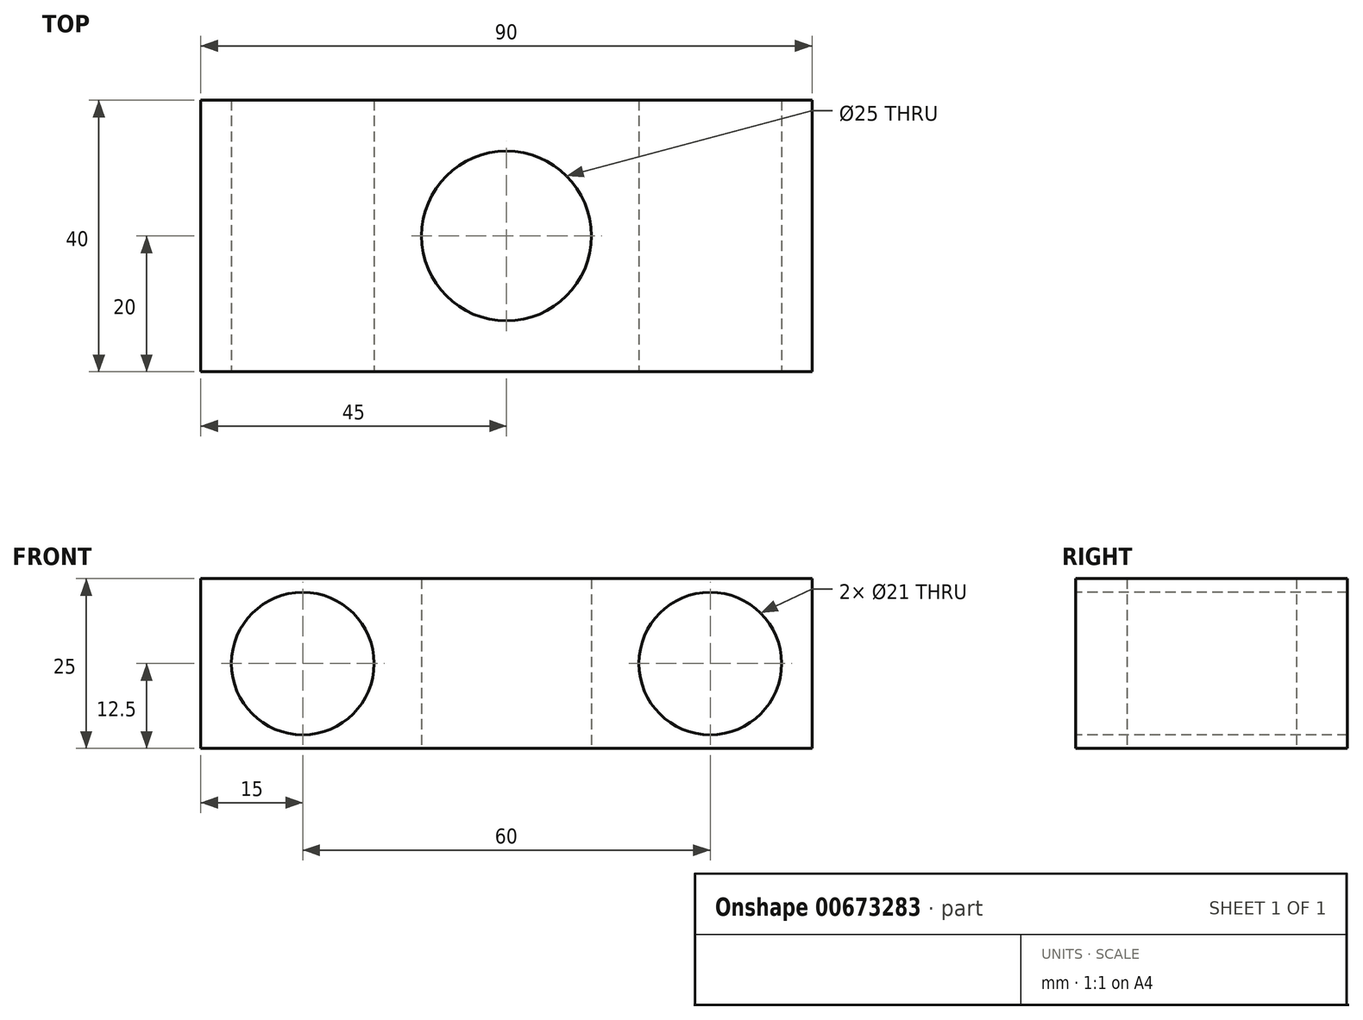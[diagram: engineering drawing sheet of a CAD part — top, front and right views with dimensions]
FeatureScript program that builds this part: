
annotation { "Feature Type Name" : "Feature", "Feature Type Description" : "" }
export const myFeature = defineFeature(function(context is Context, id is Id, definition is map)
    precondition{}
    {
        {
            var Q0;
            Q0=qCreatedBy(makeId("Top.planeOp"),FACE);
            var sketch = newSketch(context, id + "F0", { "sketchPlane" : qUnion([Q0])});
            skCircle(sketch, "E0", {"center": v(0, 0) * mm, "radius": 12.5 * mm});
            skLineSegment(sketch, "E1.bottom", {"start": v(-45, 20) * mm, "end": v(45, 20) * mm});
            skLineSegment(sketch, "E1.top", {"start": v(-45, -20) * mm, "end": v(45, -20) * mm});
            skLineSegment(sketch, "E1.left", {"start": v(-45, 20) * mm, "end": v(-45, -20) * mm});
            skLineSegment(sketch, "E1.right", {"start": v(45, 20) * mm, "end": v(45, -20) * mm});
            skLineSegment(sketch, "E2", {"start": v(0, 20) * mm, "end": v(0, -20) * mm, "construction": true});
            skLineSegment(sketch, "E3", {"start": v(45, 0) * mm, "end": v(-45, 0) * mm, "construction": true});
            skSolve(sketch);
        }
        {
            var Q0;
            Q0=makeQuery(id+"F0.imprint","IMPRINT",FACE,{"disambiguationData":[TD([[makeQuery(id+"F0.imprint","IMPRINT",EDGE,{"derivedFrom":sQuery(id+"F0.wireOp",EDGE,"E0")}),-1.0]])]});
            extrude(context, id + "F1", {"entities" : qUnion([Q0]), "depth" : 25 * mm, "offsetDistance" : 25 * mm});
        }
        {
            var Q0;
            Q0=makeQuery(id+"F1.opExtrude","SWEPT_FACE",FACE,{"disambiguationData":[OSD([sQuery(id+"F0.wireOp",EDGE,"E1.top")])]});
            var sketch = newSketch(context, id + "F2", { "sketchPlane" : qUnion([Q0])});
            skCircle(sketch, "E4", {"center": v(-30, 12.5) * mm, "radius": 10.5 * mm});
            skCircle(sketch, "E5", {"center": v(30, 12.5) * mm, "radius": 10.5 * mm});
            skLineSegment(sketch, "E6", {"start": v(-45, 12.5) * mm, "end": v(45, 12.5) * mm, "construction": true});
            skLineSegment(sketch, "E7", {"start": v(0, 25) * mm, "end": v(0, 0) * mm, "construction": true});
            skSolve(sketch);
        }
        {
            var Q0;
            Q0=makeQuery(id+"F2.imprint","IMPRINT",FACE,{"disambiguationData":[TD([[makeQuery(id+"F2.imprint","IMPRINT",EDGE,{"derivedFrom":sQuery(id+"F2.wireOp",EDGE,"E5")}),1.0]])]});
            var Q1;
            Q1=makeQuery(id+"F2.imprint","IMPRINT",FACE,{"disambiguationData":[TD([[makeQuery(id+"F2.imprint","IMPRINT",EDGE,{"derivedFrom":sQuery(id+"F2.wireOp",EDGE,"E4")}),1.0]])]});
            extrude(context, id + "F3", {"entities" : qUnion([Q0, Q1]), "operationType" : NewBodyOperationType.REMOVE, "endBound" : BoundingType.THROUGH_ALL, "oppositeDirection" : true, "depth" : 25 * mm, "offsetDistance" : 25 * mm});
        }
    });
